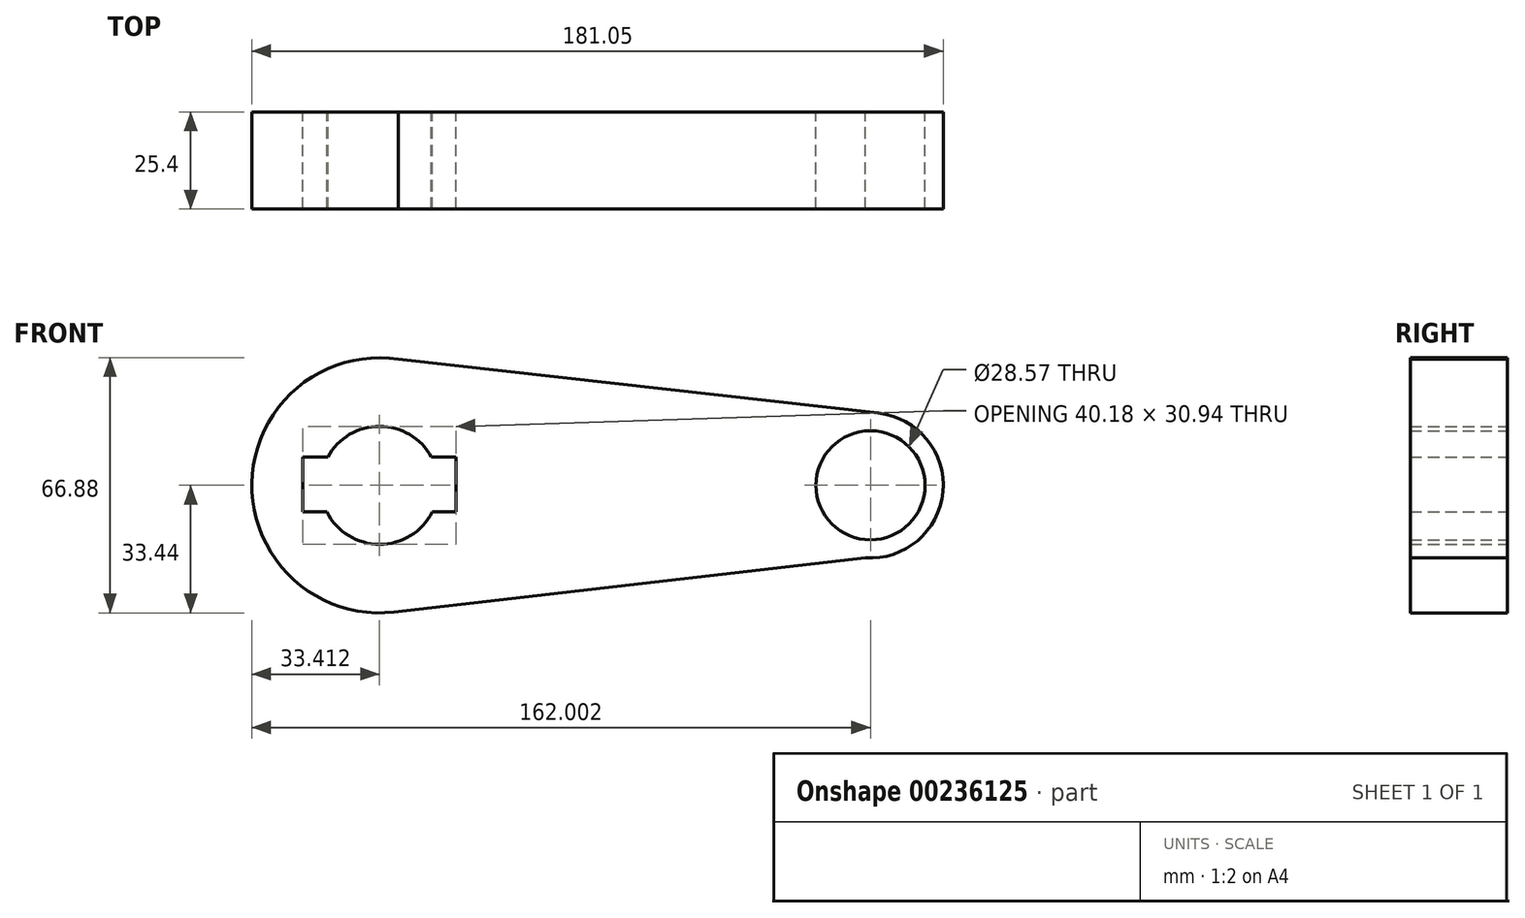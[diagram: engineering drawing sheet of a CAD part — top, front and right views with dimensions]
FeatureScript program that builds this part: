
annotation { "Feature Type Name" : "Feature", "Feature Type Description" : "" }
export const myFeature = defineFeature(function(context is Context, id is Id, definition is map)
    precondition{}
    {
        {
            var Q0;
            Q0=qCreatedBy(makeId("Front.planeOp"),FACE);
            var sketch = newSketch(context, id + "F0", { "sketchPlane" : qUnion([Q0])});
            skCircle(sketch, "E0", {"center": v(0, 0) * mm, "radius": 33.44 * mm});
            skCircle(sketch, "E1", {"center": v(128.56, 0) * mm, "radius": 19.05 * mm});
            skLineSegment(sketch, "E2", {"start": v(4.96, 33.07) * mm, "end": v(130.7, 18.93) * mm});
            skLineSegment(sketch, "E3", {"start": v(3.83, -33.22) * mm, "end": v(127.17, -19) * mm});
            skCircle(sketch, "E4", {"center": v(0, 0) * mm, "radius": 15.47 * mm});
            skCircle(sketch, "E5", {"center": v(128.56, 0) * mm, "radius": 14.29 * mm});
            skLineSegment(sketch, "E6.bottom", {"start": v(-20.12, 7.45) * mm, "end": v(20.06, 7.45) * mm});
            skLineSegment(sketch, "E6.top", {"start": v(-20.12, -7) * mm, "end": v(20.06, -7) * mm});
            skLineSegment(sketch, "E6.left", {"start": v(-20.12, 7.45) * mm, "end": v(-20.12, -7) * mm});
            skLineSegment(sketch, "E6.right", {"start": v(20.06, 7.45) * mm, "end": v(20.06, -7) * mm});
            skSolve(sketch);
        }
        {
            var Q0;
            {var subQ11=sQuery(id+"F0.wireOp",EDGE,"E6.left");Q0=makeQuery(id+"F0.imprint","IMPRINT",FACE,{"disambiguationData":[TD([[makeQuery(id+"F0.imprint","IMPRINT",EDGE,{"derivedFrom":subQ11}),-1.0]])]});}
            var Q1;
            {var subQ0=sQuery(id+"F0.wireOp",EDGE,"E2");Q1=makeQuery(id+"F0.imprint","IMPRINT",FACE,{"disambiguationData":[TD([[makeQuery(id+"F0.imprint","IMPRINT",EDGE,{"derivedFrom":subQ0}),-1.0]])]});}
            var Q2;
            Q2=makeQuery(id+"F0.imprint","IMPRINT",FACE,{"disambiguationData":[TD([[makeQuery(id+"F0.imprint","IMPRINT",EDGE,{"derivedFrom":sQuery(id+"F0.wireOp",EDGE,"E5")}),-1.0]])]});
            extrude(context, id + "F1", {"entities" : qUnion([Q0, Q1, Q2]), "depth" : 25.4 * mm});
        }
    });
